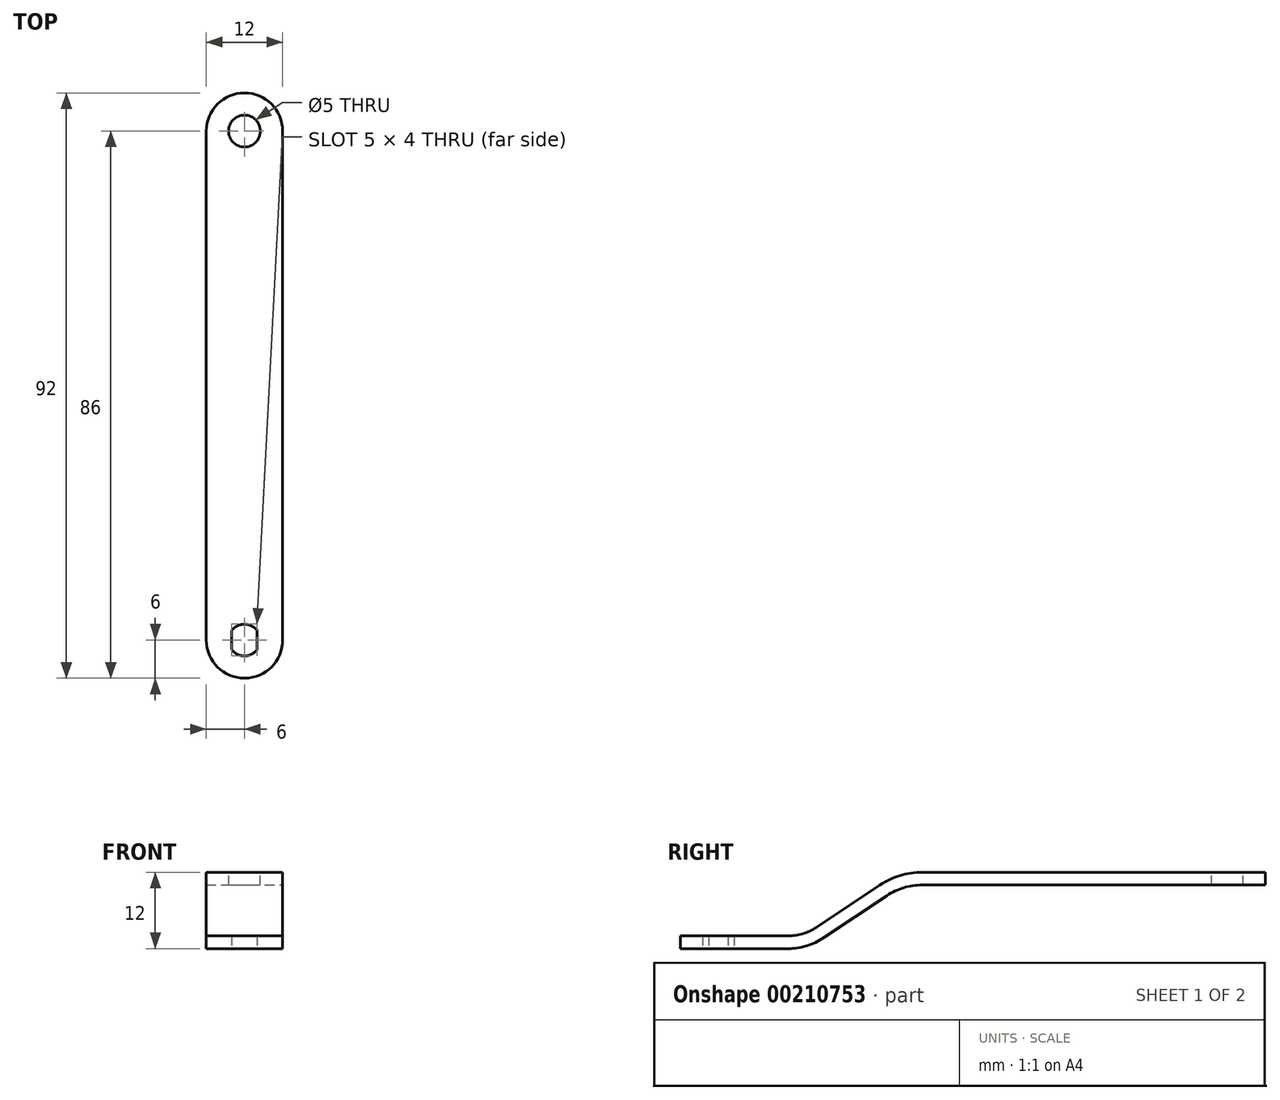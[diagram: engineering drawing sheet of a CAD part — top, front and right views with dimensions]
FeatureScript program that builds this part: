
annotation { "Feature Type Name" : "Feature", "Feature Type Description" : "" }
export const myFeature = defineFeature(function(context is Context, id is Id, definition is map)
    precondition{}
    {
        {
            var Q0;
            Q0=qCreatedBy(makeId("Right.planeOp"),FACE);
            var sketch = newSketch(context, id + "F0", { "sketchPlane" : qUnion([Q0])});
            skLineSegment(sketch, "E0", {"start": v(0, 0) * mm, "end": v(16.97, 0) * mm});
            skLineSegment(sketch, "E1", {"start": v(22.52, 1.68) * mm, "end": v(32.48, 8.32) * mm});
            skLineSegment(sketch, "E2", {"start": v(38.03, 10) * mm, "end": v(92, 10) * mm});
            skPoint(sketch, "E3.visualSharp", {"position": v(35, 10) * mm});
            skArc(sketch, "E3.filletArc", {"start": v(38.03, 10) * mm, "mid": v(35.13, 9.57) * mm, "end": v(32.48, 8.32) * mm});
            skPoint(sketch, "E4.visualSharp", {"position": v(20, 0) * mm});
            skArc(sketch, "E4.filletArc", {"start": v(16.97, 0) * mm, "mid": v(19.87, 0.43) * mm, "end": v(22.52, 1.68) * mm});
            skSolve(sketch);
        }
        {
            var Q0;
            Q0=qCreatedBy(makeId("Front.planeOp"),FACE);
            var sketch = newSketch(context, id + "F1", { "sketchPlane" : qUnion([Q0])});
            skLineSegment(sketch, "E5.bottom", {"start": v(-6, 2) * mm, "end": v(6, 2) * mm});
            skLineSegment(sketch, "E5.top", {"start": v(-6, 0) * mm, "end": v(6, 0) * mm});
            skLineSegment(sketch, "E5.left", {"start": v(-6, 2) * mm, "end": v(-6, 0) * mm});
            skLineSegment(sketch, "E5.right", {"start": v(6, 2) * mm, "end": v(6, 0) * mm});
            skSolve(sketch);
        }
        {
            var Q0;
            Q0=makeQuery(id+"F1.imprint","IMPRINT",FACE,{"disambiguationData":[TD([[makeQuery(id+"F1.imprint","IMPRINT",EDGE,{"derivedFrom":sQuery(id+"F1.wireOp",EDGE,"E5.bottom")}),-1.0]])]});
            var Q1;
            Q1=sQuery(id+"F0.wireOp",EDGE,"E0");
            var Q2;
            Q2=sQuery(id+"F0.wireOp",EDGE,"E4.filletArc");
            var Q3;
            Q3=sQuery(id+"F0.wireOp",EDGE,"E1");
            var Q4;
            Q4=sQuery(id+"F0.wireOp",EDGE,"E3.filletArc");
            var Q5;
            Q5=sQuery(id+"F0.wireOp",EDGE,"E2");
            sweep(context, id + "F2", {"profiles" : qUnion([Q0]), "path" : qUnion([Q1, Q2, Q3, Q4, Q5])});
        }
        {
            var Q0;
            Q0=qCreatedBy(makeId("Top.planeOp"),FACE);
            var sketch = newSketch(context, id + "F3", { "sketchPlane" : qUnion([Q0])});
            skCircle(sketch, "E6", {"center": v(0, 6) * mm, "radius": 2.5 * mm});
            skLineSegment(sketch, "E7", {"start": v(-2, 7.5) * mm, "end": v(-2, 4.5) * mm});
            skLineSegment(sketch, "E8", {"start": v(2, 7.5) * mm, "end": v(2, 4.5) * mm});
            skSolve(sketch);
        }
        {
            var Q0;
            {var subQ0=sQuery(id+"F3.wireOp",EDGE,"E7");Q0=makeQuery(id+"F3.imprint","IMPRINT",FACE,{"disambiguationData":[TD([[makeQuery(id+"F3.imprint","IMPRINT",EDGE,{"derivedFrom":subQ0}),1.0]])]});}
            extrude(context, id + "F4", {"entities" : qUnion([Q0]), "operationType" : NewBodyOperationType.REMOVE, "endBound" : BoundingType.UP_TO_NEXT, "depth" : 25 * mm});
        }
        {
            var Q0;
            Q0=makeQuery(id+"F2.opSweep","SWEPT_FACE",FACE,{"disambiguationData":[OSD([sQuery(id+"F0.wireOp",EDGE,"E2"),sQuery(id+"F1.wireOp",EDGE,"E5.bottom")])]});
            var sketch = newSketch(context, id + "F5", { "sketchPlane" : qUnion([Q0])});
            skCircle(sketch, "E9", {"center": v(0, 86) * mm, "radius": 2.5 * mm});
            skSolve(sketch);
        }
        {
            var Q0;
            Q0 = qSketchRegion(id + "F5", true);
            extrude(context, id + "F6", {"entities" : qUnion([Q0]), "operationType" : NewBodyOperationType.REMOVE, "endBound" : BoundingType.UP_TO_NEXT, "oppositeDirection" : true, "depth" : 25 * mm});
        }
        {
            var Q0;
            Q0=makeQuery(id+"F2.opSweep","CAP_EDGE",EDGE,{"disambiguationData":[OSD([sQuery(id+"F0.wireOp",VERTEX,"E0.start"),sQuery(id+"F1.wireOp",EDGE,"E5.right")])],"isStart":true});
            var Q1;
            Q1=makeQuery(id+"F2.opSweep","CAP_EDGE",EDGE,{"disambiguationData":[OSD([sQuery(id+"F0.wireOp",VERTEX,"E0.start"),sQuery(id+"F1.wireOp",EDGE,"E5.left")])],"isStart":true});
            fillet(context, id + "F7", {"entities" : qUnion([Q0, Q1]), "radius" : 6 * mm, "tangentPropagation" : true, "allowEdgeOverflow" : false});
        }
        {
            var Q0;
            Q0=makeQuery(id+"F2.opSweep","CAP_EDGE",EDGE,{"disambiguationData":[OSD([sQuery(id+"F0.wireOp",VERTEX,"E2.end"),sQuery(id+"F1.wireOp",EDGE,"E5.left")])],"isStart":false});
            var Q1;
            Q1=makeQuery(id+"F2.opSweep","CAP_EDGE",EDGE,{"disambiguationData":[OSD([sQuery(id+"F0.wireOp",VERTEX,"E2.end"),sQuery(id+"F1.wireOp",EDGE,"E5.right")])],"isStart":false});
            fillet(context, id + "F8", {"entities" : qUnion([Q0, Q1]), "radius" : 6 * mm, "tangentPropagation" : true, "allowEdgeOverflow" : false});
        }
    });
